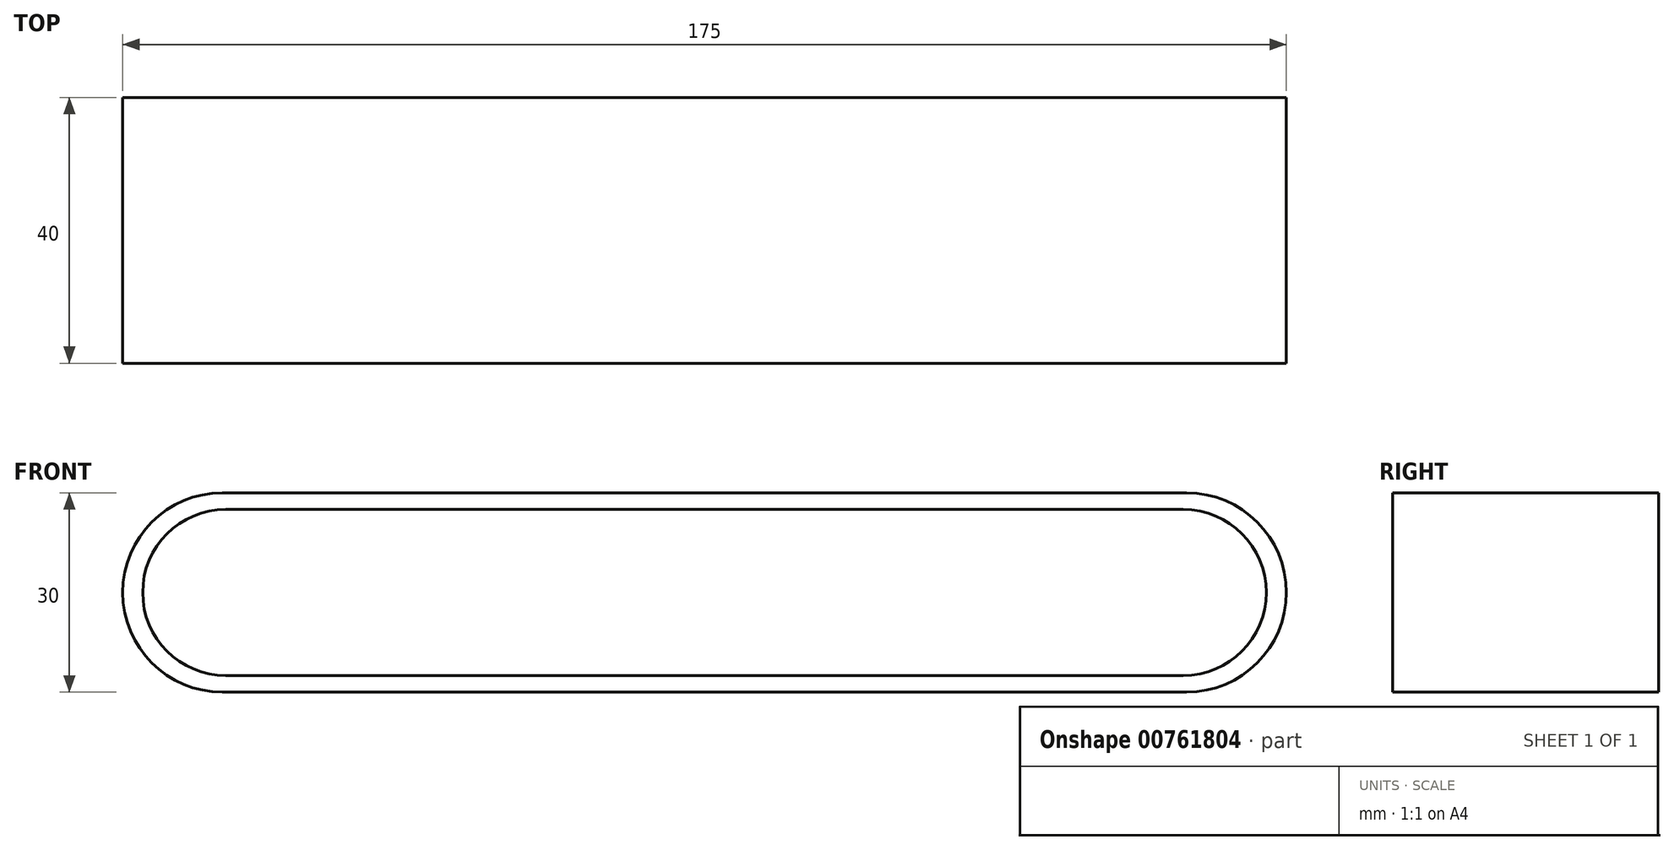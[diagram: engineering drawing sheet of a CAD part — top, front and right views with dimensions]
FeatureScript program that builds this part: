
annotation { "Feature Type Name" : "Feature", "Feature Type Description" : "" }
export const myFeature = defineFeature(function(context is Context, id is Id, definition is map)
    precondition{}
    {
        {
            var Q0;
            Q0=qCreatedBy(makeId("Top.planeOp"),FACE);
            var sketch = newSketch(context, id + "F0", { "sketchPlane" : qUnion([Q0])});
            skLineSegment(sketch, "E0.bottom", {"start": v(-87.5, -20) * mm, "end": v(87.5, -20) * mm});
            skLineSegment(sketch, "E0.top", {"start": v(-87.5, 20) * mm, "end": v(87.5, 20) * mm});
            skLineSegment(sketch, "E0.left", {"start": v(-87.5, -20) * mm, "end": v(-87.5, 20) * mm});
            skLineSegment(sketch, "E0.right", {"start": v(87.5, -20) * mm, "end": v(87.5, 20) * mm});
            skPoint(sketch, "E1", {"position": v(0, 20) * mm});
            skPoint(sketch, "E2", {"position": v(-87.5, 0) * mm});
            skSolve(sketch);
        }
        {
            var Q0;
            Q0=qSketchRegion(id+"F0",true);
            extrude(context, id + "F1", {"entities" : qUnion([Q0]), "endBound" : BoundingType.SYMMETRIC, "depth" : 30 * mm, "offsetDistance" : 25.4 * mm});
        }
        {
            var Q0;
            Q0=makeQuery(id+"F1.opExtrude","SWEPT_FACE",FACE,{"disambiguationData":[OSD([sQuery(id+"F0.wireOp",EDGE,"E0.bottom")])]});
            var sketch = newSketch(context, id + "F2", { "sketchPlane" : qUnion([Q0])});
            skCircle(sketch, "E3", {"center": v(-72.5, 0) * mm, "radius": 15 * mm});
            skPoint(sketch, "E3.centerSnap0", {"position": v(-87.5, 0) * mm});
            skCircle(sketch, "E4", {"center": v(72.5, 0) * mm, "radius": 15 * mm});
            skLineSegment(sketch, "E5.bottom", {"start": v(-72.5, 15) * mm, "end": v(72.5, 15) * mm});
            skLineSegment(sketch, "E5.top", {"start": v(-72.5, -15) * mm, "end": v(72.5, -15) * mm});
            skLineSegment(sketch, "E5.left", {"start": v(-72.5, 15) * mm, "end": v(-72.5, -15) * mm});
            skLineSegment(sketch, "E5.right", {"start": v(72.5, 15) * mm, "end": v(72.5, -15) * mm});
            skLineSegment(sketch, "E6.bottom", {"start": v(-87.5, 15) * mm, "end": v(87.5, 15) * mm});
            skLineSegment(sketch, "E6.top", {"start": v(-87.5, -15) * mm, "end": v(87.5, -15) * mm});
            skLineSegment(sketch, "E6.left", {"start": v(-87.5, 15) * mm, "end": v(-87.5, -15) * mm});
            skLineSegment(sketch, "E6.right", {"start": v(87.5, 15) * mm, "end": v(87.5, -15) * mm});
            skLineSegment(sketch, "E7.left", {"start": v(-72.5, 12.5) * mm, "end": v(-72.5, -12.5) * mm});
            skLineSegment(sketch, "E7.right", {"start": v(72.5, 12.5) * mm, "end": v(72.5, -12.5) * mm});
            skSolve(sketch);
        }
        {
            var Q0;
            {var subQ0=sQuery(id+"F2.wireOp",EDGE,"E6.bottom");var subQ3=sQuery(id+"F2.wireOp",EDGE,"E6.left");var subQ5=makeQuery(id+"F2.imprint","INTERSECT",VERTEX,{"derivedFrom":[subQ0,subQ3]});Q0=makeQuery(id+"F2.imprint","IMPRINT",FACE,{"disambiguationData":[TD([[makeQuery(id+"F2.imprint","IMPRINT",EDGE,{"disambiguationData":[TD([[subQ5,-1.0]])],"derivedFrom":subQ3}),1.0]])]});}
            var Q1;
            {var subQ0=sQuery(id+"F2.wireOp",EDGE,"E6.top");var subQ3=sQuery(id+"F2.wireOp",EDGE,"E6.left");var subQ5=makeQuery(id+"F2.imprint","INTERSECT",VERTEX,{"derivedFrom":[subQ0,subQ3]});Q1=makeQuery(id+"F2.imprint","IMPRINT",FACE,{"disambiguationData":[TD([[makeQuery(id+"F2.imprint","IMPRINT",EDGE,{"disambiguationData":[TD([[subQ5,1.0]])],"derivedFrom":subQ3}),1.0]])]});}
            var Q2;
            {var subQ0=sQuery(id+"F2.wireOp",EDGE,"E6.top");var subQ3=sQuery(id+"F2.wireOp",EDGE,"E6.right");var subQ5=makeQuery(id+"F2.imprint","INTERSECT",VERTEX,{"derivedFrom":[subQ0,subQ3]});Q2=makeQuery(id+"F2.imprint","IMPRINT",FACE,{"disambiguationData":[TD([[makeQuery(id+"F2.imprint","IMPRINT",EDGE,{"disambiguationData":[TD([[subQ5,1.0]])],"derivedFrom":subQ3}),-1.0]])]});}
            var Q3;
            {var subQ0=sQuery(id+"F2.wireOp",EDGE,"E6.bottom");var subQ3=sQuery(id+"F2.wireOp",EDGE,"E6.right");var subQ5=makeQuery(id+"F2.imprint","INTERSECT",VERTEX,{"derivedFrom":[subQ0,subQ3]});Q3=makeQuery(id+"F2.imprint","IMPRINT",FACE,{"disambiguationData":[TD([[makeQuery(id+"F2.imprint","IMPRINT",EDGE,{"disambiguationData":[TD([[subQ5,-1.0]])],"derivedFrom":subQ3}),-1.0]])]});}
            var Q4;
            {var subQ0=sQuery(id+"F2.wireOp",EDGE,"E7.bottom");var subQ1=sQuery(id+"F2.wireOp",EDGE,"E3");var subQ2=makeQuery(id+"F2.imprint","INTERSECT",VERTEX,{"derivedFrom":[subQ1,subQ0]});Q4=makeQuery(id+"F2.imprint","IMPRINT",FACE,{"disambiguationData":[TD([[makeQuery(id+"F2.imprint","IMPRINT",EDGE,{"disambiguationData":[TD([[subQ2,1.0]])],"derivedFrom":subQ1}),-1.0]])]});}
            extrude(context, id + "F3", {"entities" : qUnion([Q0, Q1, Q2, Q3, Q4]), "operationType" : NewBodyOperationType.REMOVE, "oppositeDirection" : true, "depth" : 50.8 * mm, "offsetDistance" : 25.4 * mm});
        }
        {
            var Q0;
            Q0=makeQuery(id+"F1.opExtrude","SWEPT_FACE",FACE,{"disambiguationData":[OSD([sQuery(id+"F0.wireOp",EDGE,"E0.bottom")])]});
            var sketch = newSketch(context, id + "F4", { "sketchPlane" : qUnion([Q0])});
            skLineSegment(sketch, "E8.0", {"start": v(-72, 12.5) * mm, "end": v(72, 12.5) * mm});
            skLineSegment(sketch, "E9", {"start": v(0, -12.5) * mm, "end": v(72, -12.5) * mm});
            skLineSegment(sketch, "E10", {"start": v(0, -12.5) * mm, "end": v(-72, -12.5) * mm});
            skArc(sketch, "E11", {"start": v(-72, 12.5) * mm, "mid": v(-84.5, 0) * mm, "end": v(-72, -12.5) * mm});
            skArc(sketch, "E12", {"start": v(72, 12.5) * mm, "mid": v(84.5, 0) * mm, "end": v(72, -12.5) * mm});
            skSolve(sketch);
        }
        {
            var Q0;
            Q0=makeQuery(id+"F4.imprint","IMPRINT",FACE,{"disambiguationData":[TD([[makeQuery(id+"F4.imprint","IMPRINT",EDGE,{"derivedFrom":sQuery(id+"F4.wireOp",EDGE,"E8.0")}),-1.0]])]});
            extrude(context, id + "F5", {"entities" : qUnion([Q0]), "operationType" : NewBodyOperationType.ADD, "depth" : 0 * mm, "offsetDistance" : 25 * mm});
        }
    });
